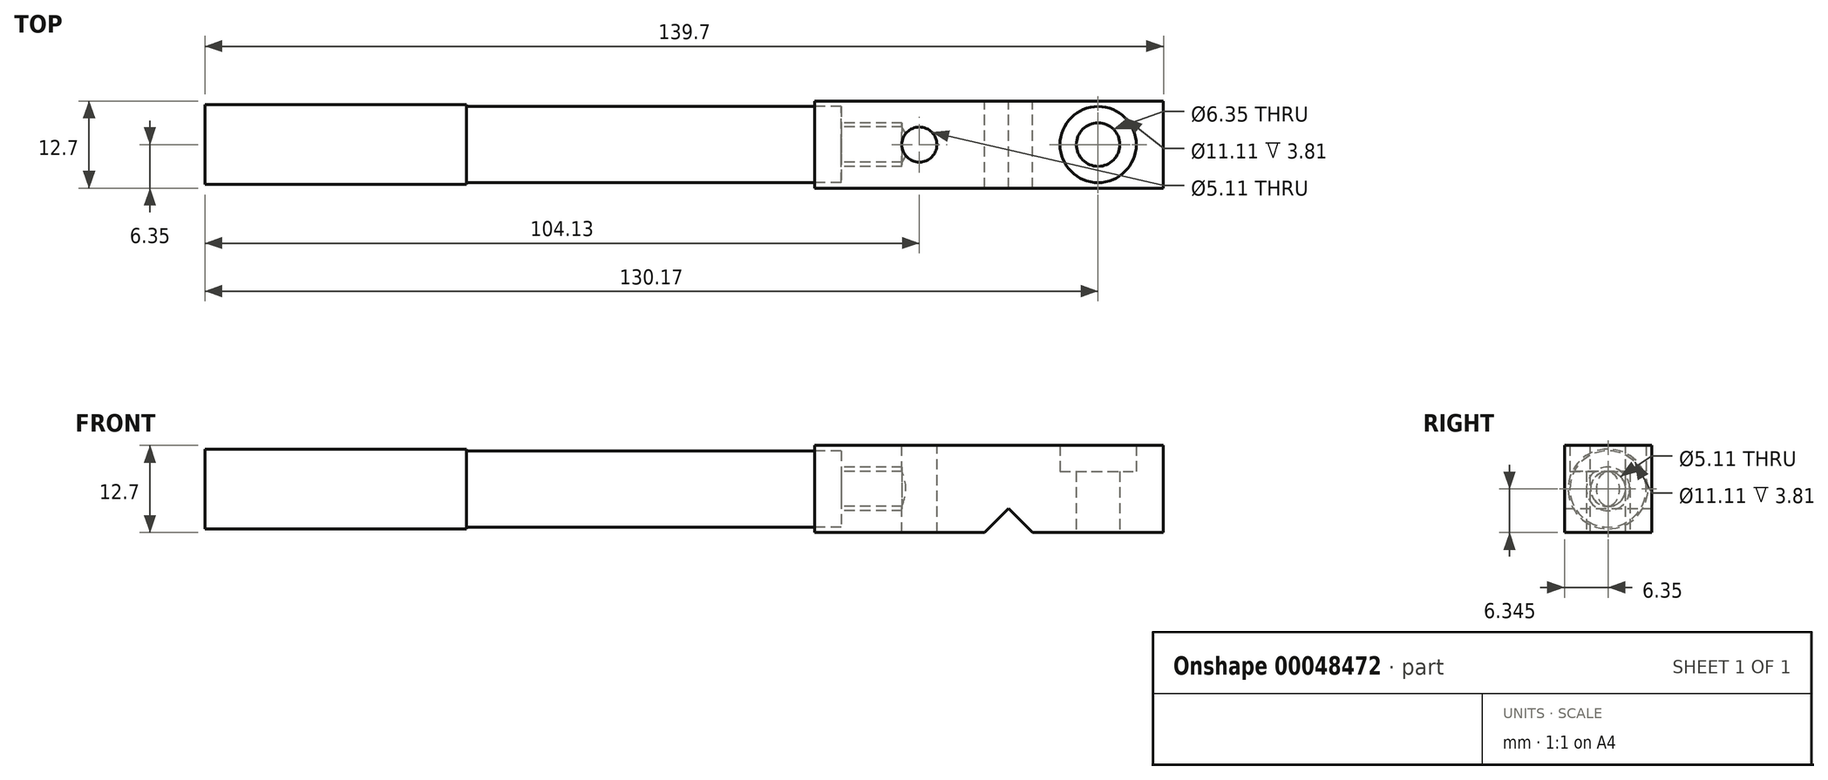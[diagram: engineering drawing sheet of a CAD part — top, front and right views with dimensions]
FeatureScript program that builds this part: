
annotation { "Feature Type Name" : "Feature", "Feature Type Description" : "" }
export const myFeature = defineFeature(function(context is Context, id is Id, definition is map)
    precondition{}
    {
        {
            var Q0;
            Q0=qCreatedBy(makeId("Front.planeOp"),FACE);
            var sketch = newSketch(context, id + "F0", { "sketchPlane" : qUnion([Q0])});
            skLineSegment(sketch, "E0", {"start": v(0, 7) * mm, "end": v(-7, 0) * mm, "construction": true});
            skLineSegment(sketch, "E1", {"start": v(-7, 0) * mm, "end": v(0, -7) * mm, "construction": true});
            skLineSegment(sketch, "E2", {"start": v(0, -7) * mm, "end": v(7, 0) * mm, "construction": true});
            skLineSegment(sketch, "E3", {"start": v(7, 0) * mm, "end": v(0, 7) * mm, "construction": true});
            skLineSegment(sketch, "E4", {"start": v(-3.5, 3.5) * mm, "end": v(-28.25, 3.5) * mm});
            skLineSegment(sketch, "E5", {"start": v(-28.25, 3.5) * mm, "end": v(-28.25, 16.2) * mm});
            skLineSegment(sketch, "E6", {"start": v(-28.25, 16.2) * mm, "end": v(22.55, 16.2) * mm});
            skLineSegment(sketch, "E7", {"start": v(22.55, 16.2) * mm, "end": v(22.55, 3.5) * mm});
            skLineSegment(sketch, "E8", {"start": v(22.55, 3.5) * mm, "end": v(3.5, 3.5) * mm});
            skLineSegment(sketch, "E9", {"start": v(-3.5, 3.5) * mm, "end": v(0, 7) * mm});
            skLineSegment(sketch, "E10", {"start": v(3.5, 3.5) * mm, "end": v(0, 7) * mm});
            skSolve(sketch);
        }
        {
            var Q0;
            Q0 = qSketchRegion(id + "F0", true);
            extrude(context, id + "F1", {"entities" : qUnion([Q0]), "endBound" : BoundingType.SYMMETRIC, "depth" : 12.7 * mm});
        }
        {
            var Q0;
            Q0=makeQuery(id+"F1.opExtrude","SWEPT_FACE",FACE,{"disambiguationData":[OSD([sQuery(id+"F0.wireOp",EDGE,"E6")])]});
            var sketch = newSketch(context, id + "F2", { "sketchPlane" : qUnion([Q0])});
            skLineSegment(sketch, "E11", {"start": v(-28.25, 0) * mm, "end": v(22.55, 0) * mm, "construction": true});
            skLineSegment(sketch, "E12", {"start": v(22.55, 6.35) * mm, "end": v(3.5, -6.35) * mm, "construction": true});
            skLineSegment(sketch, "E13.0", {"start": v(3.5, -6.35) * mm, "end": v(3.5, 6.35) * mm, "construction": true});
            skPoint(sketch, "E14", {"position": v(13.02, 0) * mm});
            skPoint(sketch, "E15.MirrorP", {"position": v(-13.02, 0) * mm});
            skCircle(sketch, "E16", {"center": v(-13.02, 0) * mm, "radius": 2.55 * mm});
            skSolve(sketch);
        }
        {
            var Q0;
            Q0=qCreatedBy(makeId("Front.planeOp"),FACE);
            var sketch = newSketch(context, id + "F3", { "sketchPlane" : qUnion([Q0])});
            skPoint(sketch, "E17.0", {"position": v(-13.02, 16.2) * mm});
            skPoint(sketch, "E17.1", {"position": v(13.02, 16.2) * mm});
            skLineSegment(sketch, "E18", {"start": v(13.02, 16.2) * mm, "end": v(13.02, 3.5) * mm});
            skLineSegment(sketch, "E19", {"start": v(13.02, 16.2) * mm, "end": v(18.58, 16.2) * mm});
            skLineSegment(sketch, "E20", {"start": v(18.58, 16.2) * mm, "end": v(18.58, 12.39) * mm});
            skLineSegment(sketch, "E21", {"start": v(18.58, 12.39) * mm, "end": v(16.2, 12.39) * mm});
            skLineSegment(sketch, "E22", {"start": v(16.2, 12.39) * mm, "end": v(16.2, 3.5) * mm});
            skLineSegment(sketch, "E23", {"start": v(16.2, 3.5) * mm, "end": v(13.02, 3.5) * mm});
            skSolve(sketch);
        }
        {
            var Q0;
            Q0 = qSketchRegion(id + "F3", true);
            var Q1;
            Q1=sQuery(id+"F3.wireOp",EDGE,"E18");
            revolve(context, id + "F4", {"operationType" : NewBodyOperationType.REMOVE, "entities" : qUnion([Q0]), "axis" : qUnion([Q1]), "revolveType" : RevolveType.FULL, "oppositeDirection" : true});
        }
        {
            var Q0;
            Q0 = qSketchRegion(id + "F2", true);
            extrude(context, id + "F5", {"entities" : qUnion([Q0]), "operationType" : NewBodyOperationType.REMOVE, "endBound" : BoundingType.THROUGH_ALL, "oppositeDirection" : true, "depth" : 25.4 * mm});
        }
        {
            var Q0;
            Q0=qCreatedBy(makeId("Front.planeOp"),FACE);
            var sketch = newSketch(context, id + "F6", { "sketchPlane" : qUnion([Q0])});
            skLineSegment(sketch, "E24", {"start": v(-28.25, 9.85) * mm, "end": v(22.55, 9.85) * mm, "construction": true});
            skLineSegment(sketch, "E25", {"start": v(-24.44, 12.4) * mm, "end": v(-15.55, 12.4) * mm});
            skLineSegment(sketch, "E26", {"start": v(-15.55, 12.4) * mm, "end": v(-14.02, 9.85) * mm});
            skLineSegment(sketch, "E27", {"start": v(-14.02, 9.85) * mm, "end": v(-28.25, 9.85) * mm});
            skLineSegment(sketch, "E28", {"start": v(-24.44, 12.4) * mm, "end": v(-24.44, 15.4) * mm});
            skLineSegment(sketch, "E29", {"start": v(-24.44, 15.4) * mm, "end": v(-28.25, 15.4) * mm});
            skLineSegment(sketch, "E30", {"start": v(-28.25, 9.85) * mm, "end": v(-28.25, 15.4) * mm});
            skSolve(sketch);
        }
        {
            var Q0;
            Q0 = qSketchRegion(id + "F6", true);
            var Q1;
            Q1=sQuery(id+"F6.wireOp",EDGE,"E27");
            revolve(context, id + "F7", {"operationType" : NewBodyOperationType.REMOVE, "entities" : qUnion([Q0]), "axis" : qUnion([Q1]), "revolveType" : RevolveType.FULL, "oppositeDirection" : true});
        }
        {
            var Q0;
            Q0=qCreatedBy(makeId("Front.planeOp"),FACE);
            var sketch = newSketch(context, id + "F8", { "sketchPlane" : qUnion([Q0])});
            skLineSegment(sketch, "E31", {"start": v(-117.15, 9.85) * mm, "end": v(-15.55, 9.85) * mm, "construction": true});
            skLineSegment(sketch, "E32", {"start": v(-15.55, 9.85) * mm, "end": v(-15.55, 13.02) * mm});
            skLineSegment(sketch, "E33", {"start": v(-15.55, 13.02) * mm, "end": v(-24.44, 13.02) * mm});
            skLineSegment(sketch, "E34", {"start": v(-24.44, 13.02) * mm, "end": v(-24.44, 15.4) * mm});
            skLineSegment(sketch, "E35", {"start": v(-24.44, 15.4) * mm, "end": v(-117.15, 15.4) * mm});
            skLineSegment(sketch, "E36", {"start": v(-117.15, 15.4) * mm, "end": v(-117.15, 9.85) * mm});
            skLineSegment(sketch, "E37.0", {"start": v(-24.44, 4.29) * mm, "end": v(-24.44, 15.4) * mm});
            skLineSegment(sketch, "E38.0", {"start": v(-24.44, 4.29) * mm, "end": v(-24.44, 15.4) * mm, "construction": true});
            skLineSegment(sketch, "E39", {"start": v(-117.15, 9.85) * mm, "end": v(-15.55, 9.85) * mm});
            skSolve(sketch);
        }
        {
            var Q0;
            Q0 = qSketchRegion(id + "F8", true);
            var Q1;
            Q1=sQuery(id+"F8.wireOp",EDGE,"E31");
            revolve(context, id + "F9", {"entities" : qUnion([Q0]), "axis" : qUnion([Q1]), "revolveType" : RevolveType.FULL});
        }
        {
            var Q0;
            Q0=qCreatedBy(makeId("Front.planeOp"),FACE);
            var sketch = newSketch(context, id + "F10", { "sketchPlane" : qUnion([Q0])});
            skLineSegment(sketch, "E40", {"start": v(-28.25, 4.29) * mm, "end": v(-117.15, 4.29) * mm, "construction": true});
            skLineSegment(sketch, "E41.0", {"start": v(-117.15, 4.29) * mm, "end": v(-117.15, 15.4) * mm, "construction": true});
            skLineSegment(sketch, "E42.0", {"start": v(-28.25, 3.5) * mm, "end": v(-28.25, 16.2) * mm, "construction": true});
            skLineSegment(sketch, "E43", {"start": v(-117.15, 15.4) * mm, "end": v(-79.05, 15.4) * mm});
            skLineSegment(sketch, "E44", {"start": v(-117.15, 9.85) * mm, "end": v(-28.25, 9.85) * mm, "construction": true});
            skLineSegment(sketch, "E45", {"start": v(-117.15, 15.4) * mm, "end": v(-117.15, 15.66) * mm});
            skLineSegment(sketch, "E46", {"start": v(-117.15, 15.66) * mm, "end": v(-79.05, 15.66) * mm});
            skLineSegment(sketch, "E47", {"start": v(-79.05, 15.66) * mm, "end": v(-79.05, 15.4) * mm});
            skSolve(sketch);
        }
        {
            var Q0;
            Q0 = qSketchRegion(id + "F10", true);
            var Q1;
            Q1=sQuery(id+"F10.wireOp",EDGE,"E44");
            revolve(context, id + "F11", {"operationType" : NewBodyOperationType.ADD, "entities" : qUnion([Q0]), "axis" : qUnion([Q1]), "revolveType" : RevolveType.FULL});
        }
    });
